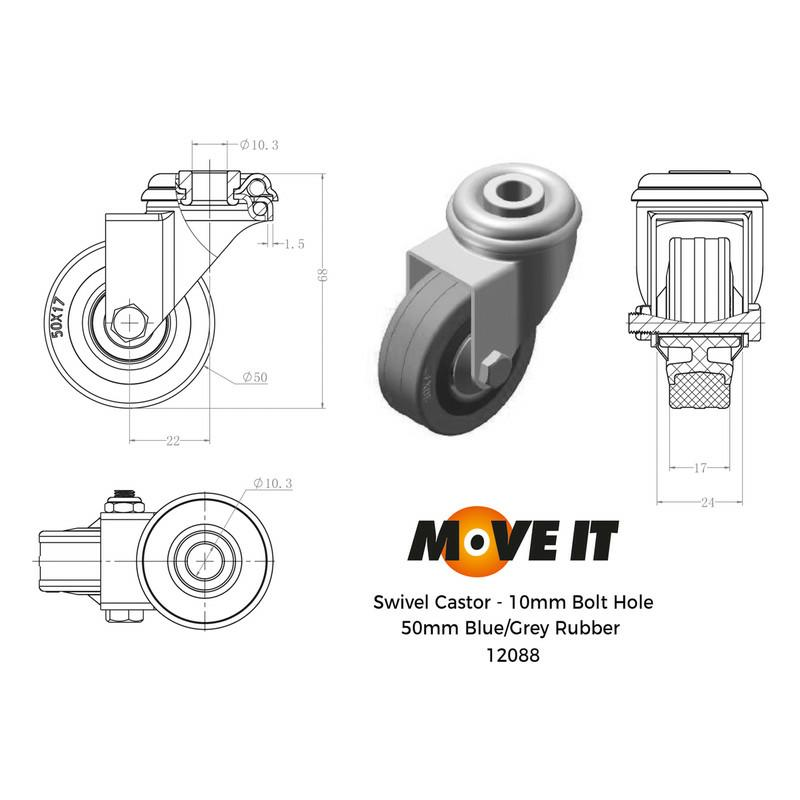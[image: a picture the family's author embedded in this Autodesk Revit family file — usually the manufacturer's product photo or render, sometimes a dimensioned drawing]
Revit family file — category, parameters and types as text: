
# Revit family: ThinkingWall Acoustic Freestander
name_source: partatom
category: Generic Models
units: mm (PartAtom-declared; Revit-internal decimal feet)

## family parameters
Always vertical = Yes
Can host rebar = No
Cut with Voids When Loaded = No
Maintain Annotation Orientation = No
Part Type = Normal
Room Calculation Point = No
Round Connector Dimension = Use Diameter
Shared = No
Work Plane-Based = No

## types (9) — shared parameters
Acoustic Colour = <By Category>
Acoustic Panel = Yes
Description = Mobile freestanding whiteboard with acoustic elements. Part of the ThinkingWall® range for flexible breakout and meeting spaces.
Manufacturer = Logovisual LTD
Model = ThinkingWall® Acoustic Freestander
Plinth Colour = <By Category>
Steel Colour = <By Category>
URL = https://www.logovisual.com
zero-valued in all types: Default Elevation

## per-type parameters (varying)
| type | Acoustic Panel 1 Heght | Acoustic Panel 2 Heght | Caster Wheel | Length | No of Slat | White Board 1 | White Board 2 |
| ThinkingWall® Acoustic Freestander 1200 Whiteboard to both sides | 600 mm  [stored 1.9685 ft] | 600 mm  [stored 1.9685 ft] | No | 1200 mm  [stored 3.93701 ft] | 29 | Yes | Yes |
| ThinkingWall® Acoustic Freestander 1500 Whiteboard to both sides | 600 mm  [stored 1.9685 ft] | 600 mm  [stored 1.9685 ft] | No | 1500 mm  [stored 4.92126 ft] | 36 | Yes | Yes |
| ThinkingWall® Acoustic Freestander 2400 Whiteboard to both sides | 600 mm  [stored 1.9685 ft] | 600 mm  [stored 1.9685 ft] | Yes | 2400 mm  [stored 7.87402 ft] | 58 | Yes | Yes |
| ThinkingWall® Acoustic Freestander 1200 Whiteboard to one side, all acoustic other side | 600 mm  [stored 1.9685 ft] | 1800 mm  [stored 5.90551 ft] | No | 1200 mm  [stored 3.93701 ft] | 29 | Yes | No |
| ThinkingWall® Acoustic Freestander 1500 Whiteboard to one side, all acoustic other side | 600 mm  [stored 1.9685 ft] | 1800 mm  [stored 5.90551 ft] | No | 1500 mm  [stored 4.92126 ft] | 36 | Yes | No |
| ThinkingWall® Acoustic Freestander 2400 Whiteboard to one side, all acoustic other side | 600 mm  [stored 1.9685 ft] | 1800 mm  [stored 5.90551 ft] | Yes | 2400 mm  [stored 7.87402 ft] | 58 | Yes | No |
| ThinkingWall® Acoustic Freestander 1200 All acoustic both sides | 1800 mm  [stored 5.90551 ft] | 1800 mm  [stored 5.90551 ft] | No | 1200 mm  [stored 3.93701 ft] | 29 | No | No |
| ThinkingWall® Acoustic Freestander 1500 All acoustic both sides | 1800 mm  [stored 5.90551 ft] | 1800 mm  [stored 5.90551 ft] | No | 1500 mm  [stored 4.92126 ft] | 36 | No | No |
| ThinkingWall® Acoustic Freestander 2400 All acoustic both sides | 1800 mm  [stored 5.90551 ft] | 1800 mm  [stored 5.90551 ft] | Yes | 2400 mm  [stored 7.87402 ft] | 58 | No | No |

note: [stored X ft] marks values corroborated as IEEE doubles in the binary element streams (Revit-internal decimal feet)

## geometry (parser evidence)
native form markers: Sweep x17
no freeform markers — native parametric forms only
